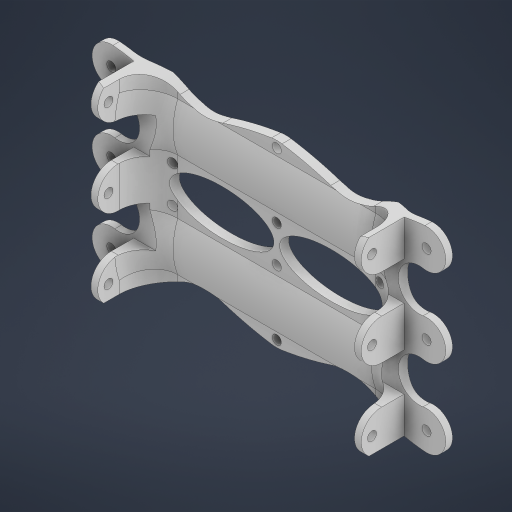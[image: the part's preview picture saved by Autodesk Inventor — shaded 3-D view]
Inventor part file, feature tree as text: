
AUTODESK INVENTOR PART (.ipt)
format: ipt  version: 2024 (Build 280153000, 153)  size: 877,056 bytes
history: native  units: mm
features: extrude x10, sketch x10, mirror x6, other x5, fillet x3
ambient origin geometry x8: Origin, YZ Plane, XZ Plane, XY Plane, X Axis, Y Axis, Z Axis, Center Point
bodies: Body1 (feature_tree)
feature tree (34):
  other  "motor_holder_down"
  other  "Твердое тело1"
  extrude  "Выдавливание1"  Depth=20.0mm
  other  "РабПлоскость1"
  extrude  "Выдавливание3"  Depth=20.0mm
  extrude  "Выдавливание8"  Depth=3.0mm
  extrude  "Выдавливание9"  Depth=90.0mm TaperAngle=0.0deg
  fillet  "Сопряжение2"  [1 undecoded]
  extrude  "Выдавливание10"  Depth=21.0mm
  fillet  "Сопряжение3"  Radius=46.0mm
  mirror  "Зеркальное отражение9"
  extrude  "Выдавливание11"  Depth=18.0mm
  extrude  "Выдавливание12"  Depth=4.0mm
  other  "РабПлоскость3"
  mirror  "Зеркальное отражение10"
  extrude  "Выдавливание13"  Depth=60.0mm
  mirror  "Зеркальное отражение11"
  mirror  "Зеркальное отражение12"
  extrude  "Выдавливание14"  Depth=50.0mm
  mirror  "Зеркальное отражение13"
  fillet  "Сопряжение4"  Radius=3.0mm
  extrude  "Выдавливание15"  Depth=23.5mm
  mirror  "Зеркальное отражение14"
  sketch  "Эскиз1"
  sketch  "Эскиз2"
  sketch  "Эскиз10"
  sketch  "Эскиз11"
  sketch  "Эскиз12"
  sketch  "Эскиз13"
  sketch  "Эскиз15"
  sketch  "Эскиз16"
  sketch  "Эскиз17"
  sketch  "Эскиз18"
  other  "ЭлементСетки3"
note: 1 required parameter value undecoded (feature->parameter linkage not recoverable at this tier; creation-order binding heuristic only, values carry confidence <= 0.55)
